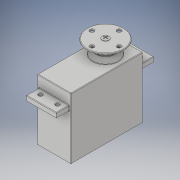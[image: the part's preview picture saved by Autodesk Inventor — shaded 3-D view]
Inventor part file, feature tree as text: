
AUTODESK INVENTOR PART (.ipt)
format: ipt  version: 2019 (Build 230136000, 136)  size: 357,376 bytes
history: native  units: mm
features: sketch x10, extrude x8, other x5, projected_geometry x3, loft x1, revolve x1, pattern_linear x1, fillet x1
ambient origin geometry x8: Origin, YZ Plane, XZ Plane, XY Plane, X Axis, Y Axis, Z Axis, Center Point
bodies: Body1 (feature_tree)
feature tree (30):
  other  "Твердое тело1"
  extrude  "Выдавливание1"  Depth=19.8mm
  other  "РабПлоскость1"
  extrude  "Выдавливание2"  Depth=42.3mm
  sketch  "Эскиз3"
  other  "РабПлоскость2"
  loft  "Лофт1"
  other  "РабПлоскость3"
  extrude  "Выдавливание3"  [1 undecoded]
  sketch  "Эскиз6"
  extrude  "Выдавливание4"  Depth=57.5mm
  extrude  "Выдавливание5"  Depth=3.0mm TaperAngle=0.0deg
  sketch  "Эскиз7"
  other  "РабПлоскость4"
  revolve  "Вращение1"
  extrude  "Выдавливание6"  Depth=1.0mm
  extrude  "Выдавливание7"  Depth=15.0mm
  extrude  "Выдавливание8"  Depth=3.0mm
  pattern_linear  "Прямоуг.массив1"  Spacing1=11.5mm  [1 undecoded]
  fillet  "Сопряжение1"  [1 undecoded]
  sketch  "Эскиз1"
  sketch  "Эскиз2"
  sketch  "Эскиз4"
  sketch  "Эскиз5"
  projected_geometry  "Спроецированная петля1"
  projected_geometry  "Спроецированная петля2"
  sketch  "Эскиз8"
  sketch  "Эскиз9"
  projected_geometry  "Спроецированная петля3"
  sketch  "Эскиз10"
note: 3 required parameter values undecoded (feature->parameter linkage not recoverable at this tier; creation-order binding heuristic only, values carry confidence <= 0.55)
